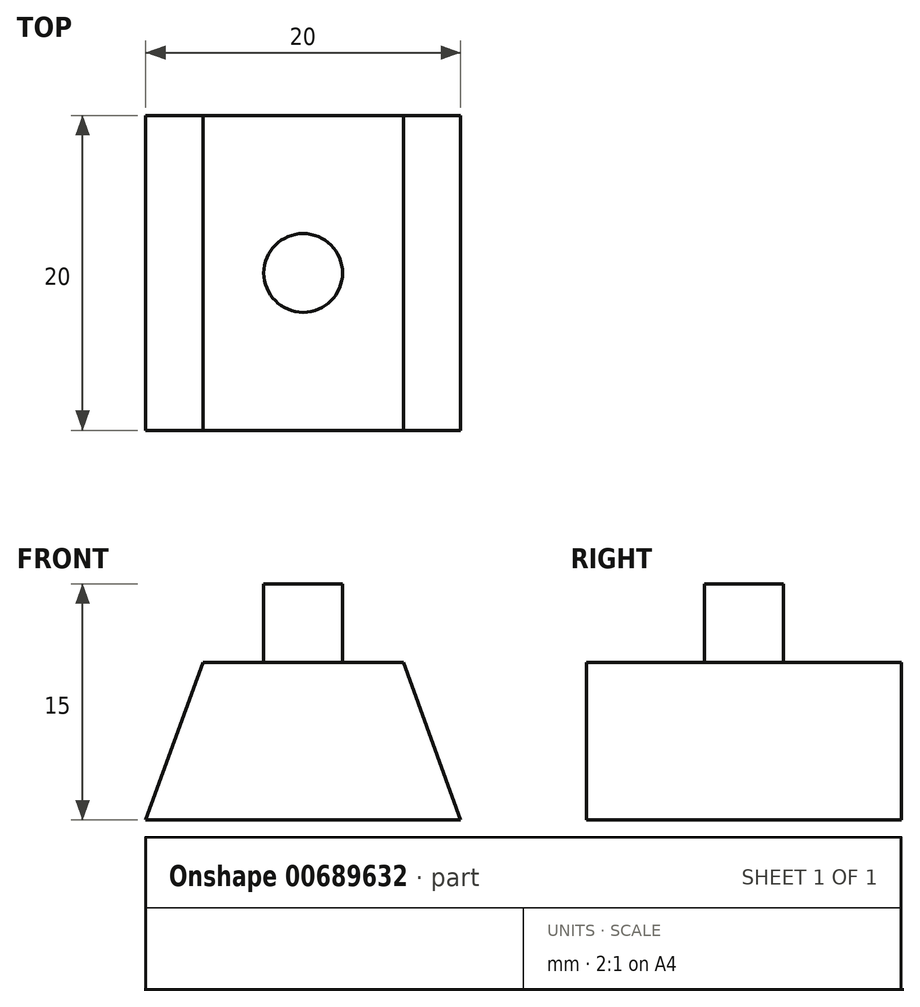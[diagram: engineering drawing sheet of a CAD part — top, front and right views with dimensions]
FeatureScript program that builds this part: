
annotation { "Feature Type Name" : "Feature", "Feature Type Description" : "" }
export const myFeature = defineFeature(function(context is Context, id is Id, definition is map)
    precondition{}
    {
        {
            var Q0;
            Q0=qCreatedBy(makeId("Front.planeOp"),FACE);
            var sketch = newSketch(context, id + "F0", { "sketchPlane" : qUnion([Q0])});
            skLineSegment(sketch, "E0", {"start": v(0, 0) * mm, "end": v(-20, 0) * mm});
            skLineSegment(sketch, "E1", {"start": v(-16.36, 10) * mm, "end": v(-3.64, 10) * mm});
            skPoint(sketch, "E2.middle", {"position": v(-10, 10) * mm});
            skLineSegment(sketch, "E3", {"start": v(-20, 0) * mm, "end": v(-16.36, 10) * mm});
            skLineSegment(sketch, "E4", {"start": v(0, 0) * mm, "end": v(-3.64, 10) * mm});
            skPoint(sketch, "E5.orphan", {"position": v(-16.36, 12.9) * mm});
            skPoint(sketch, "E6.orphan", {"position": v(-3.64, 12.9) * mm});
            skPoint(sketch, "E7.end.orphan", {"position": v(-20, 10) * mm});
            skPoint(sketch, "E8.start.orphan", {"position": v(0, 10) * mm});
            skPoint(sketch, "E2.bottom.start.orphan", {"position": v(-3.64, 7.1) * mm});
            skPoint(sketch, "E2.right.start.orphan", {"position": v(-16.36, 7.1) * mm});
            skSolve(sketch);
        }
        {
            var Q0;
            Q0=makeQuery(id+"F0.imprint","IMPRINT",FACE,{"disambiguationData":[TD([[makeQuery(id+"F0.imprint","IMPRINT",EDGE,{"derivedFrom":sQuery(id+"F0.wireOp",EDGE,"E0")}),-1.0]])]});
            extrude(context, id + "F1", {"entities" : qUnion([Q0]), "depth" : 20 * mm, "offsetDistance" : 25 * mm});
        }
        {
            var Q0;
            Q0=makeQuery(id+"F1.opExtrude","SWEPT_FACE",FACE,{"disambiguationData":[OSD([sQuery(id+"F0.wireOp",EDGE,"E1")])]});
            var sketch = newSketch(context, id + "F2", { "sketchPlane" : qUnion([Q0])});
            skCircle(sketch, "E9", {"center": v(-10, -10) * mm, "radius": 2.5 * mm});
            skPoint(sketch, "E10.orphan", {"position": v(-16.36, 0) * mm});
            skPoint(sketch, "E11.orphan", {"position": v(-3.64, -20) * mm});
            skSolve(sketch);
        }
        {
            var Q0;
            Q0=makeQuery(id+"F2.imprint","IMPRINT",FACE,{"disambiguationData":[TD([[makeQuery(id+"F2.imprint","IMPRINT",EDGE,{"derivedFrom":sQuery(id+"F2.wireOp",EDGE,"E9")}),1.0]])]});
            extrude(context, id + "F3", {"entities" : qUnion([Q0]), "operationType" : NewBodyOperationType.ADD, "depth" : 5 * mm, "offsetDistance" : 25 * mm});
        }
    });
